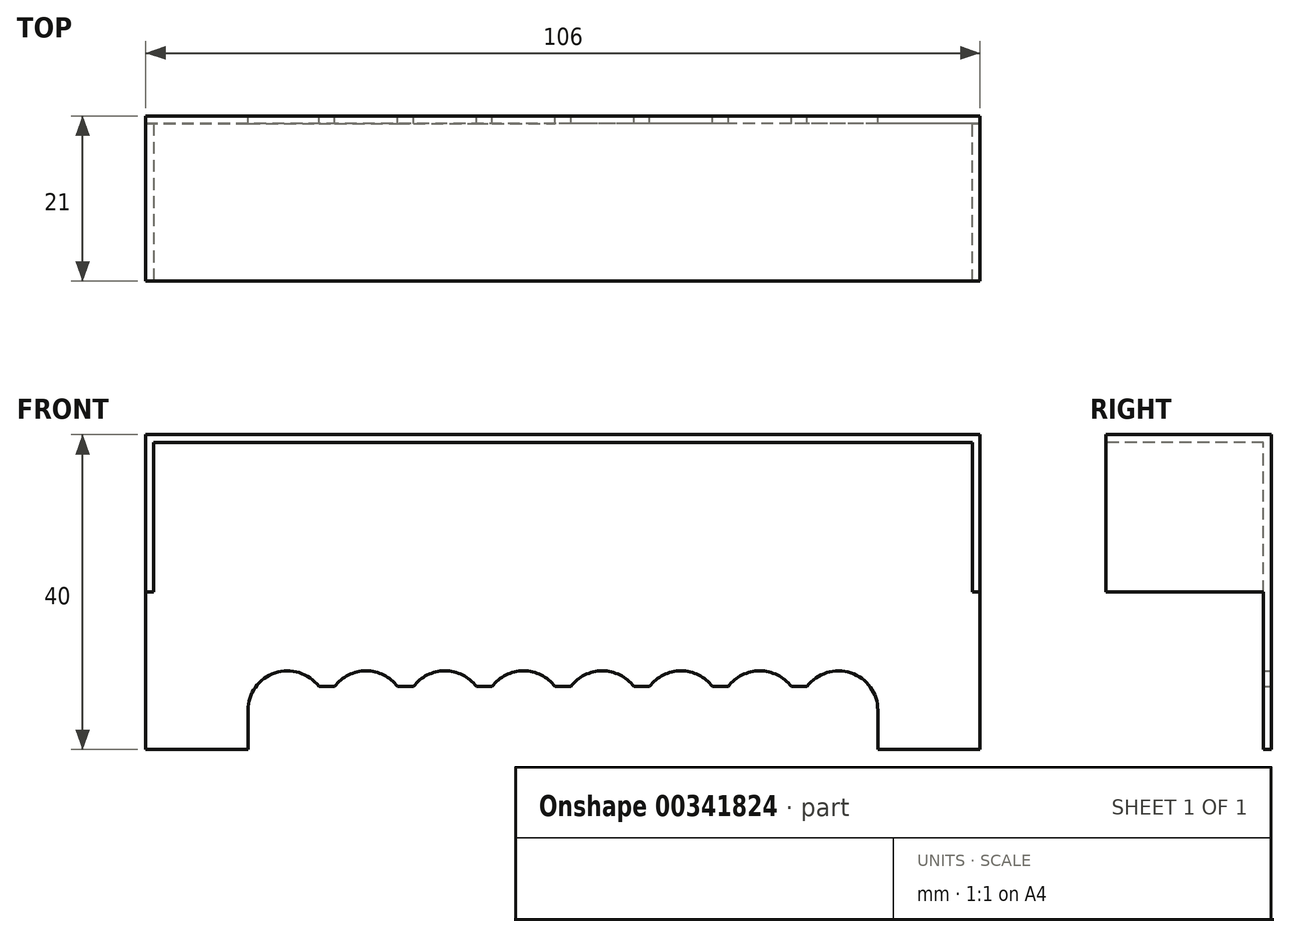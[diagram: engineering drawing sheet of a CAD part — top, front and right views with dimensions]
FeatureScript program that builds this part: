
annotation { "Feature Type Name" : "Feature", "Feature Type Description" : "" }
export const myFeature = defineFeature(function(context is Context, id is Id, definition is map)
    precondition{}
    {
        {
            var Q0;
            Q0=qCreatedBy(makeId("Right.planeOp"),FACE);
            var sketch = newSketch(context, id + "F0", { "sketchPlane" : qUnion([Q0])});
            skLineSegment(sketch, "E0", {"start": v(-21, 40) * mm, "end": v(0, 40) * mm});
            skLineSegment(sketch, "E1", {"start": v(0, 40) * mm, "end": v(0, 0) * mm});
            skLineSegment(sketch, "E2", {"start": v(0, 0) * mm, "end": v(-1, 0) * mm});
            skLineSegment(sketch, "E3", {"start": v(-1, 0) * mm, "end": v(-1, 39) * mm});
            skLineSegment(sketch, "E4", {"start": v(-1, 39) * mm, "end": v(-21, 39) * mm});
            skLineSegment(sketch, "E5", {"start": v(-21, 39) * mm, "end": v(-21, 40) * mm});
            skSolve(sketch);
        }
        {
            var Q0;
            Q0 = qSketchRegion(id + "F0", true);
            extrude(context, id + "F1", {"entities" : qUnion([Q0]), "depth" : 53 * mm});
        }
        {
            var Q0;
            Q0=makeQuery(id+"F1.opExtrude","CAP_FACE",FACE,{"disambiguationData":[OSD([sQuery(id+"F0.wireOp",EDGE,"E0"),sQuery(id+"F0.wireOp",EDGE,"E1"),sQuery(id+"F0.wireOp",EDGE,"E2"),sQuery(id+"F0.wireOp",EDGE,"E3"),sQuery(id+"F0.wireOp",EDGE,"E4"),sQuery(id+"F0.wireOp",EDGE,"E5")])],"isStart":false});
            var sketch = newSketch(context, id + "F2", { "sketchPlane" : qUnion([Q0])});
            skLineSegment(sketch, "E6.bottom", {"start": v(-21, 39) * mm, "end": v(-1, 39) * mm});
            skLineSegment(sketch, "E6.top", {"start": v(-21, 20) * mm, "end": v(-1, 20) * mm});
            skLineSegment(sketch, "E6.left", {"start": v(-21, 39) * mm, "end": v(-21, 20) * mm});
            skLineSegment(sketch, "E6.right", {"start": v(-1, 39) * mm, "end": v(-1, 20) * mm});
            skSolve(sketch);
        }
        {
            var Q0;
            Q0 = qSketchRegion(id + "F2", true);
            extrude(context, id + "F3", {"entities" : qUnion([Q0]), "oppositeDirection" : true, "depth" : 1 * mm});
        }
        {
            var Q0;
            Q0=makeQuery(id+"F1.opExtrude","SWEPT_FACE",FACE,{"disambiguationData":[OSD([sQuery(id+"F0.wireOp",EDGE,"E1")])]});
            var sketch = newSketch(context, id + "F4", { "sketchPlane" : qUnion([Q0])});
            skLineSegment(sketch, "E7.top", {"start": v(-40, 0) * mm, "end": v(0, 0) * mm});
            skLineSegment(sketch, "E7.left", {"start": v(-40, 5) * mm, "end": v(-40, 0) * mm});
            skLineSegment(sketch, "E7.right", {"start": v(0, 5) * mm, "end": v(0, 0) * mm});
            skArc(sketch, "E8", {"start": v(-31, 8) * mm, "mid": v(-36.58, 9.74) * mm, "end": v(-40, 5) * mm});
            skArc(sketch, "E9", {"start": v(-21, 8) * mm, "mid": v(-25, 10) * mm, "end": v(-29, 8) * mm});
            skArc(sketch, "E10", {"start": v(-11, 8) * mm, "mid": v(-15, 10) * mm, "end": v(-19, 8) * mm});
            skArc(sketch, "E11", {"start": v(-1, 8) * mm, "mid": v(-5, 10) * mm, "end": v(-9, 8) * mm});
            skLineSegment(sketch, "E12.bottom", {"start": v(-31, 8) * mm, "end": v(-29, 8) * mm});
            skLineSegment(sketch, "E13.trimOffspring", {"start": v(-1, 8) * mm, "end": v(0, 8) * mm});
            skLineSegment(sketch, "E14.trimOffspring", {"start": v(-11, 8) * mm, "end": v(-9, 8) * mm});
            skLineSegment(sketch, "E15.trimOffspring", {"start": v(-21, 8) * mm, "end": v(-19, 8) * mm});
            skLineSegment(sketch, "E16", {"start": v(0, 5) * mm, "end": v(0, 8) * mm});
            skSolve(sketch);
        }
        {
            var Q0;
            Q0 = qSketchRegion(id + "F4", true);
            extrude(context, id + "F5", {"entities" : qUnion([Q0]), "operationType" : NewBodyOperationType.REMOVE, "endBound" : BoundingType.UP_TO_NEXT, "oppositeDirection" : true, "depth" : 25 * mm});
        }
        {
            var Q0;
            Q0=makeQuery(id+"F3.opExtrude","SWEPT_BODY",BODY,{"disambiguationData":[OSD([sQuery(id+"F2.wireOp",EDGE,"E6.bottom"),sQuery(id+"F2.wireOp",EDGE,"E6.top"),sQuery(id+"F2.wireOp",EDGE,"E6.left"),sQuery(id+"F2.wireOp",EDGE,"E6.right")])]});
            var Q1;
            Q1=makeQuery(id+"F1.opExtrude","SWEPT_BODY",BODY,{"disambiguationData":[OSD([sQuery(id+"F0.wireOp",EDGE,"E0"),sQuery(id+"F0.wireOp",EDGE,"E1"),sQuery(id+"F0.wireOp",EDGE,"E2"),sQuery(id+"F0.wireOp",EDGE,"E3"),sQuery(id+"F0.wireOp",EDGE,"E4"),sQuery(id+"F0.wireOp",EDGE,"E5")])]});
            var Q2;
            Q2=qCreatedBy(makeId("Right.planeOp"),FACE);
            mirror(context, id + "F6", {"operationType" : NewBodyOperationType.ADD, "entities" : qUnion([Q0, Q1]), "mirrorPlane" : qUnion([Q2])});
        }
    });
